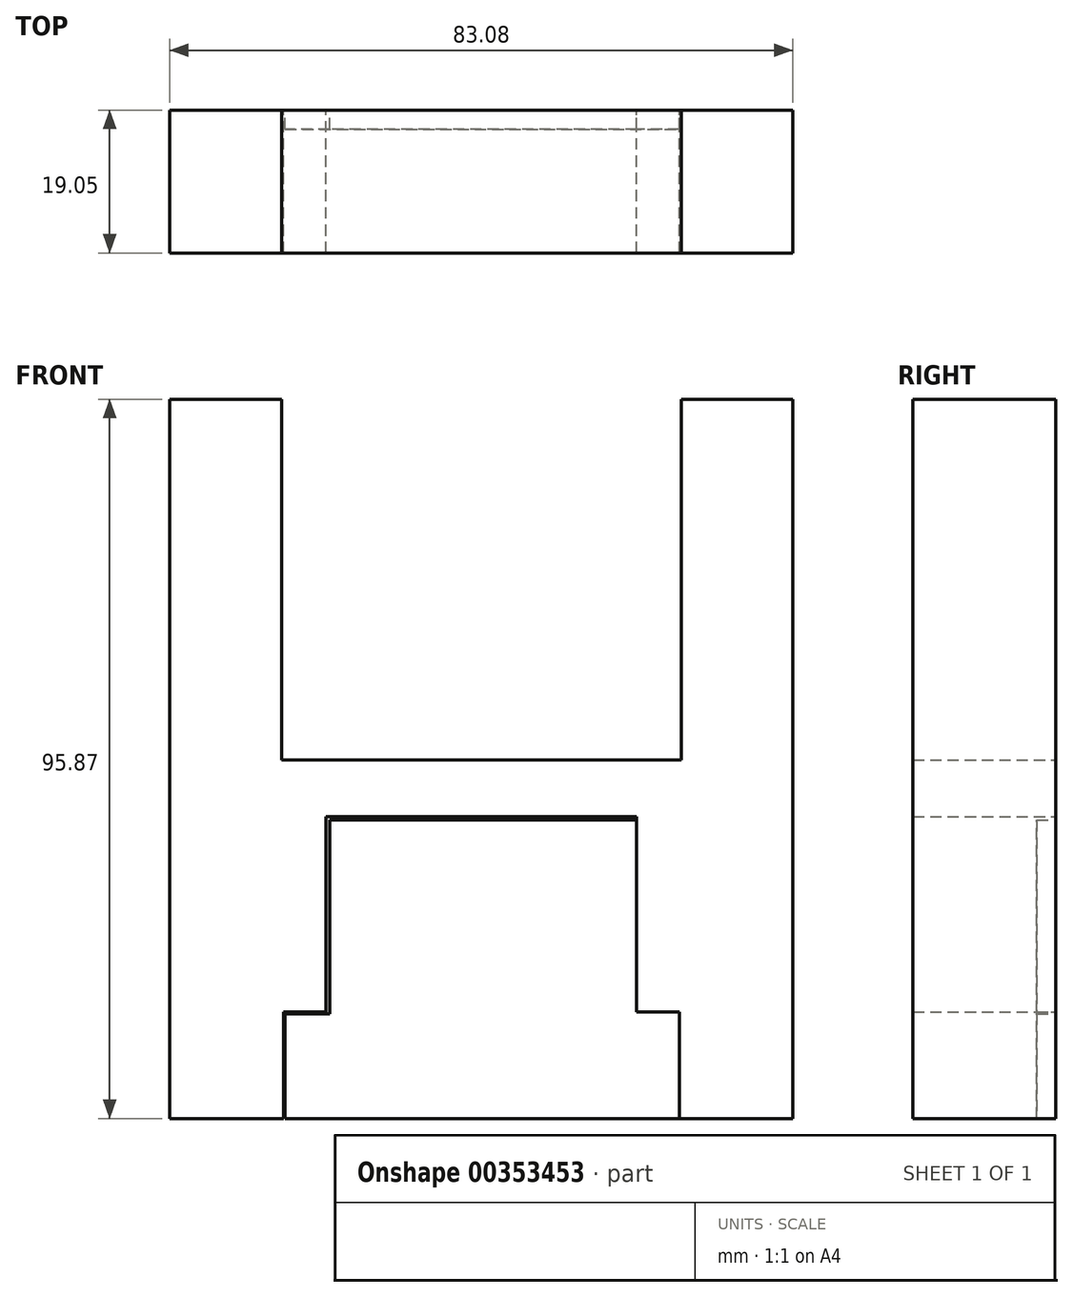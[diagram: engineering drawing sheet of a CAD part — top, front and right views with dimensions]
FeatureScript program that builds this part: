
annotation { "Feature Type Name" : "Feature", "Feature Type Description" : "" }
export const myFeature = defineFeature(function(context is Context, id is Id, definition is map)
    precondition{}
    {
        {
            var Q0;
            Q0=qCreatedBy(makeId("Front.planeOp"),FACE);
            var sketch = newSketch(context, id + "F0", { "sketchPlane" : qUnion([Q0])});
            skLineSegment(sketch, "E0", {"start": v(-43.08, 48.05) * mm, "end": v(-43.08, -47.82) * mm});
            skLineSegment(sketch, "E1", {"start": v(-43.08, -47.82) * mm, "end": v(-27.93, -47.82) * mm});
            skLineSegment(sketch, "E2", {"start": v(-27.93, -47.82) * mm, "end": v(-27.93, -33.61) * mm});
            skLineSegment(sketch, "E3", {"start": v(-27.93, -33.61) * mm, "end": v(-22.25, -33.61) * mm});
            skLineSegment(sketch, "E4", {"start": v(-22.25, -33.61) * mm, "end": v(-22.25, -7.57) * mm});
            skLineSegment(sketch, "E5", {"start": v(-22.25, -7.57) * mm, "end": v(19.17, -7.57) * mm});
            skLineSegment(sketch, "E6", {"start": v(19.17, -7.57) * mm, "end": v(19.17, -33.61) * mm});
            skLineSegment(sketch, "E7", {"start": v(19.17, -33.61) * mm, "end": v(24.86, -33.61) * mm});
            skLineSegment(sketch, "E8", {"start": v(24.86, -33.61) * mm, "end": v(24.86, -47.82) * mm});
            skLineSegment(sketch, "E9", {"start": v(24.86, -47.82) * mm, "end": v(40, -47.82) * mm});
            skLineSegment(sketch, "E10", {"start": v(40, -47.82) * mm, "end": v(40, 48.05) * mm});
            skLineSegment(sketch, "E11", {"start": v(40, 48.05) * mm, "end": v(25.1, 48.05) * mm});
            skLineSegment(sketch, "E12", {"start": v(25.1, 48.05) * mm, "end": v(25.1, 0) * mm});
            skLineSegment(sketch, "E13", {"start": v(25.1, 0) * mm, "end": v(-28.17, 0) * mm});
            skLineSegment(sketch, "E14", {"start": v(-28.17, 0) * mm, "end": v(-28.17, 48.05) * mm});
            skLineSegment(sketch, "E15", {"start": v(-28.17, 48.05) * mm, "end": v(-43.08, 48.05) * mm});
            skSolve(sketch);
        }
        {
            var Q0;
            Q0 = qSketchRegion(id + "F0", true);
            extrude(context, id + "F1", {"entities" : qUnion([Q0]), "depth" : 19.05 * mm});
        }
        {
            var Q0;
            Q0=qCreatedBy(makeId("Front.planeOp"),FACE);
            var sketch = newSketch(context, id + "F2", { "sketchPlane" : qUnion([Q0])});
            skLineSegment(sketch, "E16", {"start": v(-27.7, -47.82) * mm, "end": v(24.86, -47.82) * mm});
            skLineSegment(sketch, "E17", {"start": v(24.86, -47.82) * mm, "end": v(24.86, -33.61) * mm});
            skLineSegment(sketch, "E18", {"start": v(24.86, -33.61) * mm, "end": v(19.17, -33.61) * mm});
            skLineSegment(sketch, "E19", {"start": v(19.17, -33.61) * mm, "end": v(19.17, -8.05) * mm});
            skLineSegment(sketch, "E20", {"start": v(19.17, -8.05) * mm, "end": v(-21.78, -8.05) * mm});
            skLineSegment(sketch, "E21", {"start": v(-21.78, -8.05) * mm, "end": v(-21.78, -33.85) * mm});
            skLineSegment(sketch, "E22", {"start": v(-21.78, -33.85) * mm, "end": v(-27.7, -33.85) * mm});
            skLineSegment(sketch, "E23", {"start": v(-27.7, -33.85) * mm, "end": v(-27.7, -47.82) * mm});
            skSolve(sketch);
        }
        {
            var Q0;
            Q0=makeQuery(id+"F2.imprint","IMPRINT",FACE,{"disambiguationData":[TD([[makeQuery(id+"F2.imprint","IMPRINT",EDGE,{"derivedFrom":sQuery(id+"F2.wireOp",EDGE,"E16")}),1.0]])]});
            extrude(context, id + "F3", {"entities" : qUnion([Q0]), "depth" : 2.54 * mm});
        }
    });
